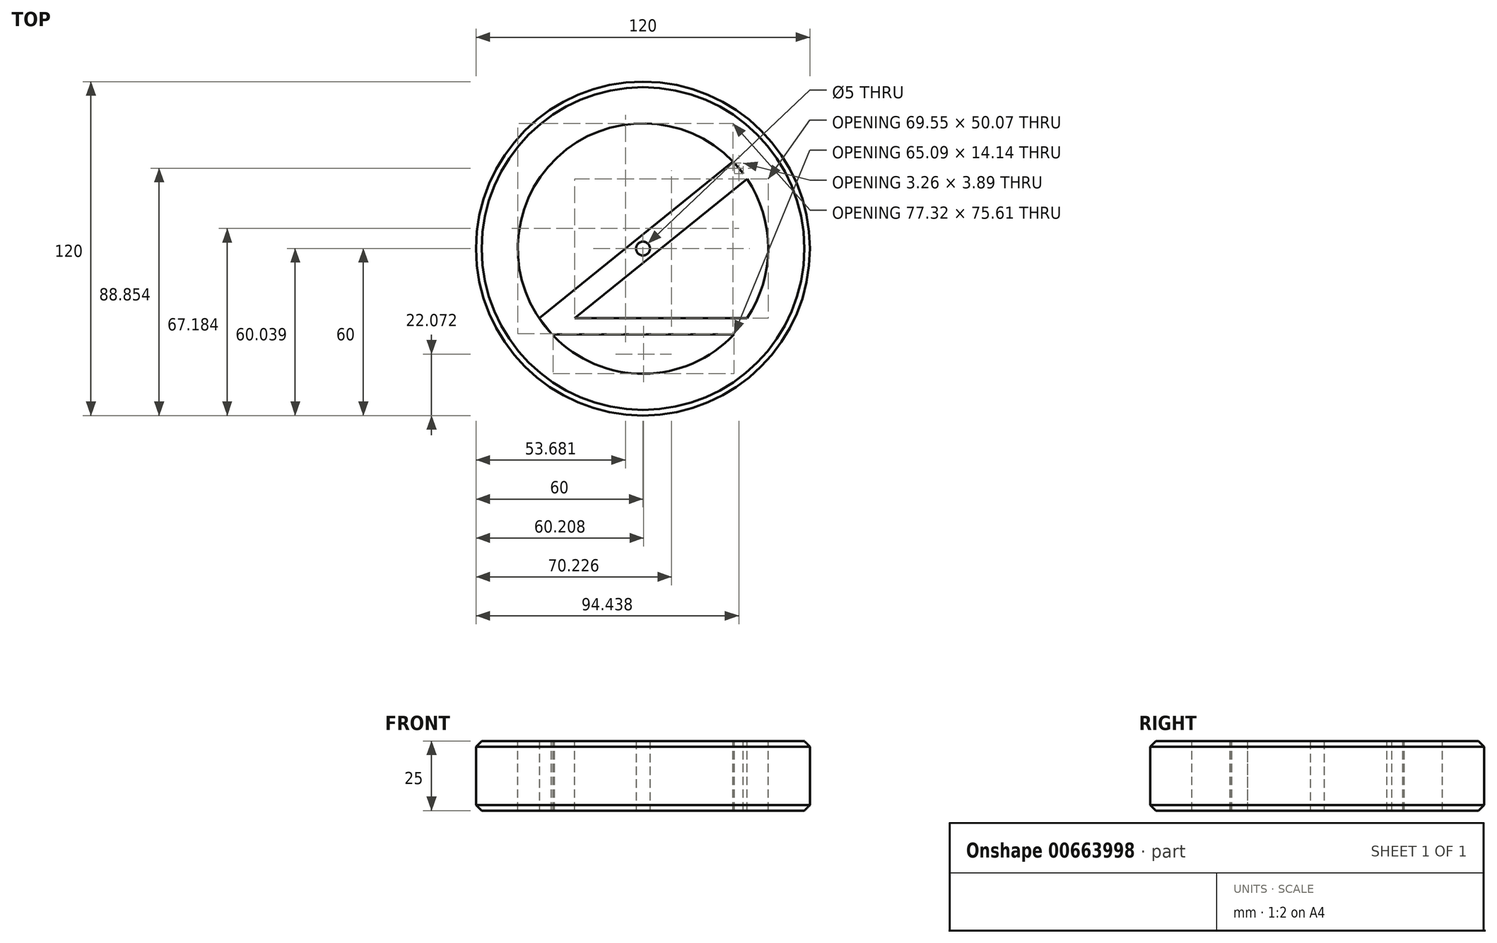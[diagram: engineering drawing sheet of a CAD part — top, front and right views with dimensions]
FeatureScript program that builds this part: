
annotation { "Feature Type Name" : "Feature", "Feature Type Description" : "" }
export const myFeature = defineFeature(function(context is Context, id is Id, definition is map)
    precondition{}
    {
        {
            var Q0;
            Q0=qCreatedBy(makeId("Top.planeOp"),FACE);
            var sketch = newSketch(context, id + "F0", { "sketchPlane" : qUnion([Q0])});
            skCircle(sketch, "E0", {"center": v(0, 0) * mm, "radius": 60 * mm});
            skCircle(sketch, "E1", {"center": v(0, 0) * mm, "radius": 45 * mm});
            skSolve(sketch);
        }
        {
            var Q0;
            Q0=makeQuery(id+"F0.imprint","IMPRINT",FACE,{"disambiguationData":[TD([[makeQuery(id+"F0.imprint","IMPRINT",EDGE,{"derivedFrom":sQuery(id+"F0.wireOp",EDGE,"E0")}),1.0]])]});
            extrude(context, id + "F1", {"entities" : qUnion([Q0]), "endBound" : BoundingType.SYMMETRIC, "oppositeDirection" : true, "depth" : 25 * mm, "offsetDistance" : 25 * mm});
        }
        {
            var Q0;
            Q0=makeQuery(id+"F1.opExtrude","CAP_EDGE",EDGE,{"disambiguationData":[OSD([sQuery(id+"F0.wireOp",EDGE,"E0")])],"isStart":true});
            var Q1;
            Q1=makeQuery(id+"F1.opExtrude","CAP_EDGE",EDGE,{"disambiguationData":[OSD([sQuery(id+"F0.wireOp",EDGE,"E0")])],"isStart":false});
            chamfer(context, id + "F2", {"entities" : qUnion([Q0, Q1]), "width" : 2 * mm, "tangentPropagation" : true});
        }
        {
            var Q0;
            Q0=qCreatedBy(makeId("Top.planeOp"),FACE);
            var sketch = newSketch(context, id + "F3", { "sketchPlane" : qUnion([Q0])});
            skLineSegment(sketch, "E2", {"start": v(32.37, 31.32) * mm, "end": v(-37.3, -25.02) * mm});
            skLineSegment(sketch, "E3", {"start": v(37.51, 25.19) * mm, "end": v(-32.41, -31.35) * mm});
            skLineSegment(sketch, "E4", {"start": v(37.51, 25.19) * mm, "end": v(32.37, 31.32) * mm});
            skLineSegment(sketch, "E5", {"start": v(-32.41, -31.35) * mm, "end": v(-37.3, -25.02) * mm});
            skCircle(sketch, "E6", {"center": v(0, 0) * mm, "radius": 2.5 * mm});
            skSolve(sketch);
        }
        {
            var Q0;
            Q0 = qSketchRegion(id + "F3", true);
            extrude(context, id + "F4", {"entities" : qUnion([Q0]), "operationType" : NewBodyOperationType.ADD, "endBound" : BoundingType.SYMMETRIC, "depth" : 25 * mm, "offsetDistance" : 25 * mm});
        }
        {
            var Q0;
            Q0=makeQuery(id+"F0.imprint","IMPRINT",FACE,{"disambiguationData":[TD([[makeQuery(id+"F0.imprint","IMPRINT",EDGE,{"derivedFrom":sQuery(id+"F0.wireOp",EDGE,"E1")}),1.0]])]});
            var sketch = newSketch(context, id + "F5", { "sketchPlane" : qUnion([Q0])});
            skLineSegment(sketch, "E7", {"start": v(-24.71, -25) * mm, "end": v(38.12, -25) * mm});
            skLineSegment(sketch, "E8", {"start": v(-31.97, -30.86) * mm, "end": v(32.81, -30.86) * mm});
            skLineSegment(sketch, "E9", {"start": v(32.81, -30.86) * mm, "end": v(38.12, -25) * mm});
            skLineSegment(sketch, "E10", {"start": v(-24.71, -25) * mm, "end": v(-31.97, -30.86) * mm});
            skSolve(sketch);
        }
        {
            var Q0;
            Q0 = qSketchRegion(id + "F5", true);
            extrude(context, id + "F6", {"entities" : qUnion([Q0]), "operationType" : NewBodyOperationType.ADD, "endBound" : BoundingType.SYMMETRIC, "depth" : 25 * mm, "offsetDistance" : 25 * mm});
        }
    });
